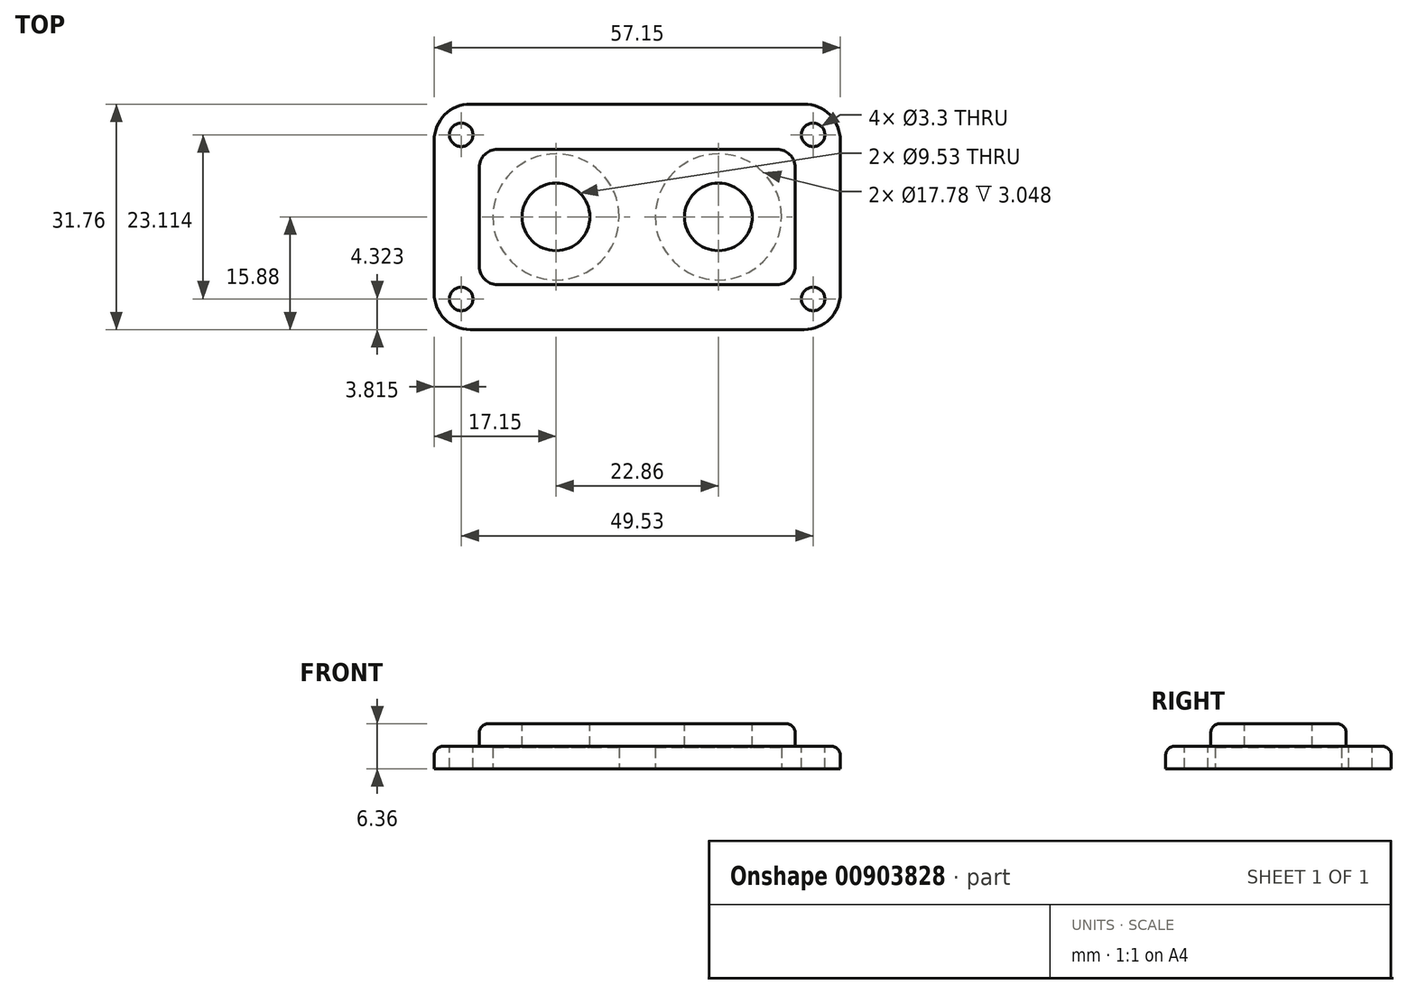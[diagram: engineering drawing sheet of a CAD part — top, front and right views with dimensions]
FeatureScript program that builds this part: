
annotation { "Feature Type Name" : "Feature", "Feature Type Description" : "" }
export const myFeature = defineFeature(function(context is Context, id is Id, definition is map)
    precondition{}
    {
        {
            var Q0;
            Q0=qCreatedBy(makeId("Top.planeOp"),FACE);
            var sketch = newSketch(context, id + "F0", { "sketchPlane" : qUnion([Q0])});
            skLineSegment(sketch, "E0.bottom", {"start": v(23.5, -15.87) * mm, "end": v(-23.5, -15.88) * mm});
            skLineSegment(sketch, "E0.top", {"start": v(23.5, 15.88) * mm, "end": v(-23.5, 15.87) * mm});
            skLineSegment(sketch, "E0.left", {"start": v(28.57, -10.8) * mm, "end": v(28.57, 10.8) * mm});
            skLineSegment(sketch, "E0.right", {"start": v(-28.58, -10.8) * mm, "end": v(-28.58, 10.8) * mm});
            skPoint(sketch, "E0.middle", {"position": v(0, 0) * mm});
            skLineSegment(sketch, "E1", {"start": v(0, 0) * mm, "end": v(-11.43, 0) * mm, "construction": true});
            skCircle(sketch, "E2", {"center": v(-11.43, 0) * mm, "radius": 4.76 * mm});
            skCircle(sketch, "E3.MirrorC", {"center": v(11.43, 0) * mm, "radius": 4.76 * mm});
            skLineSegment(sketch, "E4.0", {"start": v(19.68, 9.53) * mm, "end": v(-19.69, 9.52) * mm});
            skLineSegment(sketch, "E4.1", {"start": v(22.22, -6.98) * mm, "end": v(22.22, 6.99) * mm});
            skLineSegment(sketch, "E4.2", {"start": v(19.68, -9.52) * mm, "end": v(-19.69, -9.53) * mm});
            skLineSegment(sketch, "E4.3", {"start": v(-22.23, -6.99) * mm, "end": v(-22.23, 6.98) * mm});
            skPoint(sketch, "E5.visualSharp", {"position": v(-28.58, 15.87) * mm});
            skArc(sketch, "E5.filletArc", {"start": v(-23.5, 15.87) * mm, "mid": v(-27.09, 14.39) * mm, "end": v(-28.58, 10.8) * mm});
            skPoint(sketch, "E6.visualSharp", {"position": v(-22.23, 9.52) * mm});
            skArc(sketch, "E6.filletArc", {"start": v(-19.69, 9.52) * mm, "mid": v(-21.48, 8.78) * mm, "end": v(-22.23, 6.98) * mm});
            skPoint(sketch, "E7.visualSharp", {"position": v(-22.23, -9.53) * mm});
            skArc(sketch, "E7.filletArc", {"start": v(-22.23, -6.99) * mm, "mid": v(-21.48, -8.78) * mm, "end": v(-19.69, -9.53) * mm});
            skPoint(sketch, "E8.visualSharp", {"position": v(22.22, -9.52) * mm});
            skArc(sketch, "E8.filletArc", {"start": v(19.68, -9.52) * mm, "mid": v(21.48, -8.78) * mm, "end": v(22.22, -6.98) * mm});
            skPoint(sketch, "E9.visualSharp", {"position": v(22.22, 9.53) * mm});
            skArc(sketch, "E9.filletArc", {"start": v(22.22, 6.99) * mm, "mid": v(21.48, 8.78) * mm, "end": v(19.68, 9.53) * mm});
            skPoint(sketch, "E10.visualSharp", {"position": v(28.57, 15.88) * mm});
            skArc(sketch, "E10.filletArc", {"start": v(28.58, 10.8) * mm, "mid": v(27.09, 14.39) * mm, "end": v(23.5, 15.88) * mm});
            skPoint(sketch, "E11.visualSharp", {"position": v(-28.58, -15.88) * mm});
            skArc(sketch, "E11.filletArc", {"start": v(-28.58, -10.8) * mm, "mid": v(-27.09, -14.39) * mm, "end": v(-23.5, -15.88) * mm});
            skPoint(sketch, "E12.visualSharp", {"position": v(28.57, -15.87) * mm});
            skArc(sketch, "E12.filletArc", {"start": v(23.5, -15.87) * mm, "mid": v(27.09, -14.39) * mm, "end": v(28.57, -10.8) * mm});
            skLineSegment(sketch, "E13", {"start": v(0, 9.52) * mm, "end": v(0, 11.56) * mm, "construction": true});
            skLineSegment(sketch, "E14", {"start": v(0, 11.56) * mm, "end": v(-24.77, 11.56) * mm, "construction": true});
            skCircle(sketch, "E15", {"center": v(-24.77, 11.56) * mm, "radius": 1.65 * mm});
            skCircle(sketch, "E16.MirrorC", {"center": v(24.77, 11.56) * mm, "radius": 1.65 * mm});
            skCircle(sketch, "E17.MirrorC", {"center": v(-24.77, -11.56) * mm, "radius": 1.65 * mm});
            skCircle(sketch, "E18.MirrorC", {"center": v(24.77, -11.56) * mm, "radius": 1.65 * mm});
            skSolve(sketch);
        }
        {
            var Q0;
            Q0=makeQuery(id+"F0.imprint","IMPRINT",FACE,{"disambiguationData":[TD([[makeQuery(id+"F0.imprint","IMPRINT",EDGE,{"derivedFrom":sQuery(id+"F0.wireOp",EDGE,"E0.bottom")}),-1.0]])]});
            var Q1;
            Q1=makeQuery(id+"F0.imprint","IMPRINT",FACE,{"disambiguationData":[TD([[makeQuery(id+"F0.imprint","IMPRINT",EDGE,{"derivedFrom":sQuery(id+"F0.wireOp",EDGE,"E2")}),-1.0]])]});
            extrude(context, id + "F1", {"entities" : qUnion([Q0, Q1]), "oppositeDirection" : true, "depth" : 3.17 * mm, "offsetDistance" : 25.4 * mm});
        }
        {
            var Q0;
            Q0=makeQuery(id+"F0.imprint","IMPRINT",FACE,{"disambiguationData":[TD([[makeQuery(id+"F0.imprint","IMPRINT",EDGE,{"derivedFrom":sQuery(id+"F0.wireOp",EDGE,"E2")}),-1.0]])]});
            extrude(context, id + "F2", {"entities" : qUnion([Q0]), "operationType" : NewBodyOperationType.ADD, "depth" : 3.17 * mm, "offsetDistance" : 25.4 * mm});
        }
        {
            var Q0;
            Q0=makeQuery(id+"F2.opExtrude","CAP_EDGE",EDGE,{"disambiguationData":[OSD([sQuery(id+"F0.wireOp",EDGE,"E4.0")])],"isStart":false});
            var Q1;
            Q1=makeQuery(id+"F1.opExtrude","CAP_EDGE",EDGE,{"disambiguationData":[OSD([sQuery(id+"F0.wireOp",EDGE,"E0.top")])],"isStart":true});
            fillet(context, id + "F3", {"entities" : qUnion([Q0, Q1]), "tangentPropagation" : true, "radius" : 1.27 * mm, "defaultsChanged" : false, "vertexSettings" : [], "allowEdgeOverflow" : false});
        }
        {
            var Q0;
            Q0=makeQuery(id+"F1.opExtrude","CAP_FACE",FACE,{"disambiguationData":[OSD([sQuery(id+"F0.wireOp",EDGE,"E0.bottom"),sQuery(id+"F0.wireOp",EDGE,"E0.top"),sQuery(id+"F0.wireOp",EDGE,"E0.left"),sQuery(id+"F0.wireOp",EDGE,"E0.right"),sQuery(id+"F0.wireOp",EDGE,"E2"),sQuery(id+"F0.wireOp",EDGE,"E3.MirrorC"),sQuery(id+"F0.wireOp",EDGE,"E5.filletArc"),sQuery(id+"F0.wireOp",EDGE,"E10.filletArc"),sQuery(id+"F0.wireOp",EDGE,"E11.filletArc"),sQuery(id+"F0.wireOp",EDGE,"E12.filletArc")])],"isStart":false});
            var sketch = newSketch(context, id + "F4", { "sketchPlane" : qUnion([Q0])});
            skCircle(sketch, "E19", {"center": v(-11.43, 0) * mm, "radius": 8.9 * mm});
            skCircle(sketch, "E20.MirrorC", {"center": v(11.43, 0) * mm, "radius": 8.9 * mm});
            skSolve(sketch);
        }
        {
            var Q0;
            Q0 = qSketchRegion(id + "F4", true);
            extrude(context, id + "F5", {"entities" : qUnion([Q0]), "operationType" : NewBodyOperationType.REMOVE, "oppositeDirection" : true, "depth" : 3.05 * mm, "offsetDistance" : 25.4 * mm});
        }
    });
